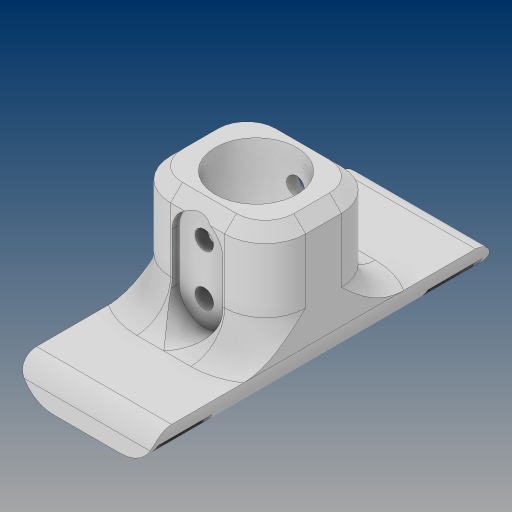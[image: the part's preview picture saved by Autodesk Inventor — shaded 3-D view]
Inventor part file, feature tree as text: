
AUTODESK INVENTOR PART (.ipt)
format: ipt  version: 2023 (Build 270158000, 158)  size: 623,104 bytes
history: native  units: mm
features: extrude x10, sketch x6, fillet x3, mirror x2, plane x1, chamfer x1
ambient origin geometry x8: Origin, YZ Plane, XZ Plane, XY Plane, X Axis, Y Axis, Z Axis, Center Point
bodies: Solid1 (feature_tree)
feature tree (23):
  sketch  "Sketch1"  dims[d0=50.0mm d1=100.0mm d2=300.0mm d3=20.0mm d4=10.0mm d5=2.0mm d6=0.5mm d7=0.5mm d8=70.0mm d9=15.0mm d10=15.0mm d11=15.0mm d12=15.0mm d13=12.8mm d14=12.8mm d15=12.8mm d16=1.0mm d17=1.0mm d18=2.0mm d19=30.0mm d20=2.0mm d21=30.0mm d22=2.0mm d23=40.595mm d24=2.5mm d25=30.0deg d26=60.0deg d27=220.451928mm d28=1.1mm d29=12.632665mm d30=120.0deg d31=20.0mm d32=0.0mm]
  extrude  "Extrusion1"  Depth=10.0mm TaperAngle=0.0deg
  extrude  "Extrusion2"  Depth=7.5mm
  sketch  "Sketch2"  dims[d33=7.5mm d34=0.0mm d35=7.5mm]
  extrude  "Extrusion3"  Depth=15.0mm
  extrude  "Extrusion4"  Depth=5.5mm
  plane  "Work Plane1"
  mirror  "Mirror1"
  mirror  "Mirror2"
  fillet  "Fillet1"  Radius=5.5mm
  sketch  "Sketch3"  dims[d36=7.5mm d37=15.0mm]
  extrude  "Extrusion5"  Depth=12.0mm TaperAngle=0.0deg
  extrude  "Extrusion6"  Depth=10.0mm
  sketch  "Sketch4"  dims[d38=15.0mm d39=5.5mm d40=5.5mm]
  extrude  "Extrusion7"  Depth=10.0mm
  fillet  "Fillet2"  Radius=50.0mm
  fillet  "Fillet3"  Radius=19.5mm
  chamfer  "Chamfer1"  Distance=24.15mm
  extrude  "Extrusion8"  Depth=10.0mm TaperAngle=0.0deg
  extrude  "Extrusion9"  Depth=10.0mm
  extrude  "Extrusion10"  Depth=10.0mm
  sketch  "Sketch5"  dims[d41=2.0mm d42=0.0mm d43=12.0mm d44=0.0mm]
  sketch  "Sketch6"  dims[d45=12.0mm d46=18.5mm d47=8.0mm d48=50.0mm d49=0.0mm d50=19.5mm d51=0.0mm d52=24.15mm d53=2.1mm d54=0.0mm d55=10.0mm d56=5.0mm d57=3.5mm d58=2.0mm d59=45.0deg d60=0.2mm d61=0.0mm d62=30.0mm d63=0.0mm d64=22.0mm d65=0.0mm]
